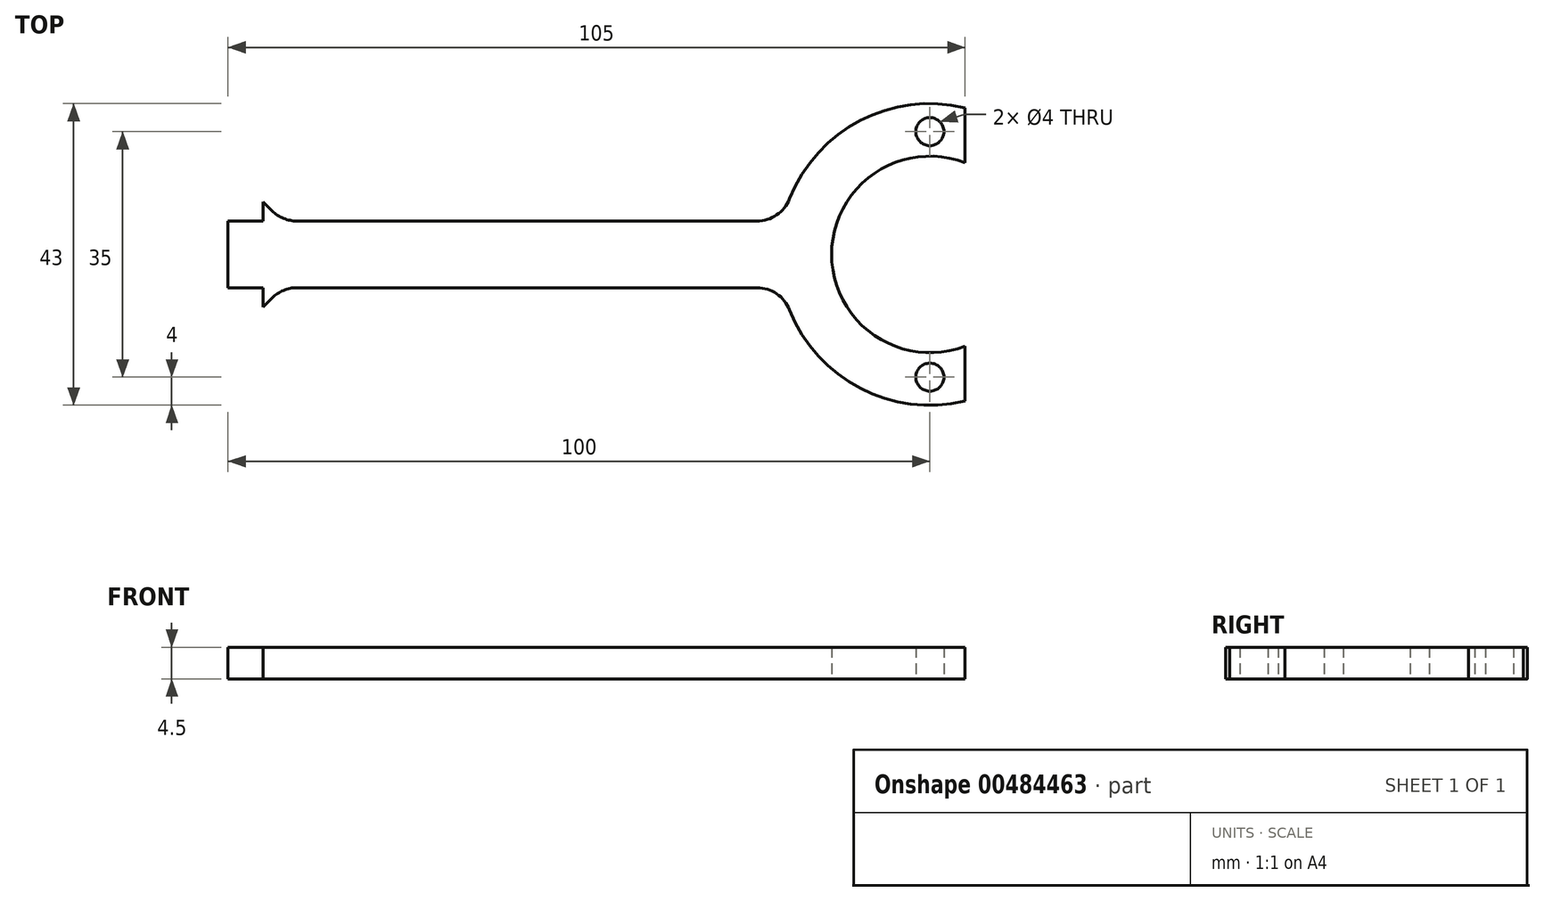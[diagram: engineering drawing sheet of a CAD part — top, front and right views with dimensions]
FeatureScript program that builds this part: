
annotation { "Feature Type Name" : "Feature", "Feature Type Description" : "" }
export const myFeature = defineFeature(function(context is Context, id is Id, definition is map)
    precondition{}
    {
        {
            var Q0;
            Q0=qCreatedBy(makeId("Top.planeOp"),FACE);
            var sketch = newSketch(context, id + "F0", { "sketchPlane" : qUnion([Q0])});
            skLineSegment(sketch, "E0.bottom", {"start": v(-50, 4.75) * mm, "end": v(50, 4.75) * mm});
            skLineSegment(sketch, "E0.top", {"start": v(-50, -4.75) * mm, "end": v(50, -4.75) * mm});
            skLineSegment(sketch, "E0.left", {"start": v(-50, 4.75) * mm, "end": v(-50, -4.75) * mm});
            skLineSegment(sketch, "E0.right", {"start": v(50, 4.75) * mm, "end": v(50, -4.75) * mm});
            skCircle(sketch, "E1", {"center": v(50, 0) * mm, "radius": 14 * mm});
            skCircle(sketch, "E2", {"center": v(50, 0) * mm, "radius": 21.5 * mm});
            skLineSegment(sketch, "E3", {"start": v(50, 39.25) * mm, "end": v(50, -32.9) * mm});
            skCircle(sketch, "E4", {"center": v(50, 17.5) * mm, "radius": 2 * mm});
            skCircle(sketch, "E5", {"center": v(50, -17.5) * mm, "radius": 2 * mm});
            skLineSegment(sketch, "E6", {"start": v(55, 39.07) * mm, "end": v(55, -32.83) * mm});
            skLineSegment(sketch, "E7", {"start": v(-45, 7.5) * mm, "end": v(-45, -7.5) * mm});
            skLineSegment(sketch, "E8", {"start": v(-45, -7.5) * mm, "end": v(-37.5, 0) * mm});
            skLineSegment(sketch, "E9", {"start": v(-37.5, 0) * mm, "end": v(-45, 7.5) * mm});
            skSolve(sketch);
        }
        {
            var Q0;
            {var subQ0=sQuery(id+"F0.wireOp",EDGE,"E0.left");Q0=makeQuery(id+"F0.imprint","IMPRINT",FACE,{"disambiguationData":[TD([[makeQuery(id+"F0.imprint","IMPRINT",EDGE,{"derivedFrom":subQ0}),1.0]])]});}
            var Q1;
            {var subQ0=sQuery(id+"F0.wireOp",EDGE,"E2");var subQ1=sQuery(id+"F0.wireOp",EDGE,"E0.bottom");var subQ2=makeQuery(id+"F0.imprint","INTERSECT",VERTEX,{"derivedFrom":[subQ1,subQ0]});Q1=makeQuery(id+"F0.imprint","IMPRINT",FACE,{"disambiguationData":[TD([[makeQuery(id+"F0.imprint","IMPRINT",EDGE,{"disambiguationData":[TD([[subQ2,-1.0]])],"derivedFrom":subQ1}),-1.0]])]});}
            var Q2;
            {var subQ1=sQuery(id+"F0.wireOp",EDGE,"E2");var subQ6=sQuery(id+"F0.wireOp",EDGE,"E0.bottom");var subQ9=makeQuery(id+"F0.imprint","INTERSECT",VERTEX,{"derivedFrom":[subQ6,subQ1]});Q2=makeQuery(id+"F0.imprint","IMPRINT",FACE,{"disambiguationData":[TD([[makeQuery(id+"F0.imprint","IMPRINT",EDGE,{"disambiguationData":[TD([[subQ9,-1.0]])],"derivedFrom":subQ6}),1.0]])]});}
            var Q3;
            {var subQ1=sQuery(id+"F0.wireOp",EDGE,"E2");var subQ3=sQuery(id+"F0.wireOp",EDGE,"E0.top");var subQ4=makeQuery(id+"F0.imprint","INTERSECT",VERTEX,{"derivedFrom":[subQ3,subQ1]});Q3=makeQuery(id+"F0.imprint","IMPRINT",FACE,{"disambiguationData":[TD([[makeQuery(id+"F0.imprint","IMPRINT",EDGE,{"disambiguationData":[TD([[subQ4,-1.0]])],"derivedFrom":subQ3}),-1.0]])]});}
            var Q4;
            {var subQ0=sQuery(id+"F0.wireOp",EDGE,"E3");var subQ1=sQuery(id+"F0.wireOp",EDGE,"E1");var subQ2=makeQuery(id+"F0.imprint","INTERSECT",VERTEX,{"disambiguationData":[OD(1.0)],"derivedFrom":[subQ1,subQ0]});Q4=makeQuery(id+"F0.imprint","IMPRINT",FACE,{"disambiguationData":[TD([[makeQuery(id+"F0.imprint","IMPRINT",EDGE,{"disambiguationData":[TD([[subQ2,-1.0]])],"derivedFrom":subQ1}),-1.0]])]});}
            var Q5;
            {var subQ0=sQuery(id+"F0.wireOp",EDGE,"E3");var subQ1=sQuery(id+"F0.wireOp",EDGE,"E1");var subQ2=makeQuery(id+"F0.imprint","INTERSECT",VERTEX,{"disambiguationData":[OD(0.0)],"derivedFrom":[subQ1,subQ0]});Q5=makeQuery(id+"F0.imprint","IMPRINT",FACE,{"disambiguationData":[TD([[makeQuery(id+"F0.imprint","IMPRINT",EDGE,{"disambiguationData":[TD([[subQ2,1.0]])],"derivedFrom":subQ1}),-1.0]])]});}
            var Q6;
            {var subQ0=sQuery(id+"F0.wireOp",EDGE,"E9");var subQ6=sQuery(id+"F0.wireOp",EDGE,"E0.bottom");var subQ9=makeQuery(id+"F0.imprint","INTERSECT",VERTEX,{"derivedFrom":[subQ6,subQ0]});Q6=makeQuery(id+"F0.imprint","IMPRINT",FACE,{"disambiguationData":[TD([[makeQuery(id+"F0.imprint","IMPRINT",EDGE,{"disambiguationData":[TD([[subQ9,-1.0]])],"derivedFrom":subQ6}),-1.0]])]});}
            var Q7;
            {var subQ5=sQuery(id+"F0.wireOp",EDGE,"E7");var subQ6=sQuery(id+"F0.wireOp",EDGE,"E0.bottom");var subQ7=makeQuery(id+"F0.imprint","INTERSECT",VERTEX,{"derivedFrom":[subQ6,subQ5]});Q7=makeQuery(id+"F0.imprint","IMPRINT",FACE,{"disambiguationData":[TD([[makeQuery(id+"F0.imprint","IMPRINT",EDGE,{"disambiguationData":[TD([[subQ7,-1.0]])],"derivedFrom":subQ6}),-1.0]])]});}
            var Q8;
            {var subQ0=sQuery(id+"F0.wireOp",EDGE,"E7");var subQ1=sQuery(id+"F0.wireOp",EDGE,"E0.bottom");var subQ2=makeQuery(id+"F0.imprint","INTERSECT",VERTEX,{"derivedFrom":[subQ1,subQ0]});Q8=makeQuery(id+"F0.imprint","IMPRINT",FACE,{"disambiguationData":[TD([[makeQuery(id+"F0.imprint","IMPRINT",EDGE,{"disambiguationData":[TD([[subQ2,-1.0]])],"derivedFrom":subQ1}),1.0]])]});}
            var Q9;
            {var subQ0=sQuery(id+"F0.wireOp",EDGE,"E7");var subQ1=sQuery(id+"F0.wireOp",EDGE,"E0.top");var subQ2=makeQuery(id+"F0.imprint","INTERSECT",VERTEX,{"derivedFrom":[subQ1,subQ0]});Q9=makeQuery(id+"F0.imprint","IMPRINT",FACE,{"disambiguationData":[TD([[makeQuery(id+"F0.imprint","IMPRINT",EDGE,{"disambiguationData":[TD([[subQ2,-1.0]])],"derivedFrom":subQ1}),-1.0]])]});}
            extrude(context, id + "F1", {"entities" : qUnion([Q0, Q1, Q2, Q3, Q4, Q5, Q6, Q7, Q8, Q9]), "depth" : 4.5 * mm});
        }
        {
            var Q0;
            Q0=makeQuery(id+"F1.opExtrude","SWEPT_EDGE",EDGE,{"disambiguationData":[OSD([sQuery(id+"F0.wireOp",EDGE,"E0.top"),sQuery(id+"F0.wireOp",EDGE,"E2")])]});
            var Q1;
            Q1=makeQuery(id+"F1.opExtrude","SWEPT_EDGE",EDGE,{"disambiguationData":[OSD([sQuery(id+"F0.wireOp",EDGE,"E0.bottom"),sQuery(id+"F0.wireOp",EDGE,"E2")])]});
            var Q2;
            Q2=makeQuery(id+"F1.opExtrude","SWEPT_EDGE",EDGE,{"disambiguationData":[OSD([sQuery(id+"F0.wireOp",EDGE,"E0.top"),sQuery(id+"F0.wireOp",EDGE,"E8")])]});
            var Q3;
            Q3=makeQuery(id+"F1.opExtrude","SWEPT_EDGE",EDGE,{"disambiguationData":[OSD([sQuery(id+"F0.wireOp",EDGE,"E0.bottom"),sQuery(id+"F0.wireOp",EDGE,"E9")])]});
            fillet(context, id + "F2", {"entities" : qUnion([Q0, Q1, Q2, Q3]), "radius" : 5 * mm, "tangentPropagation" : true, "allowEdgeOverflow" : false});
        }
    });
